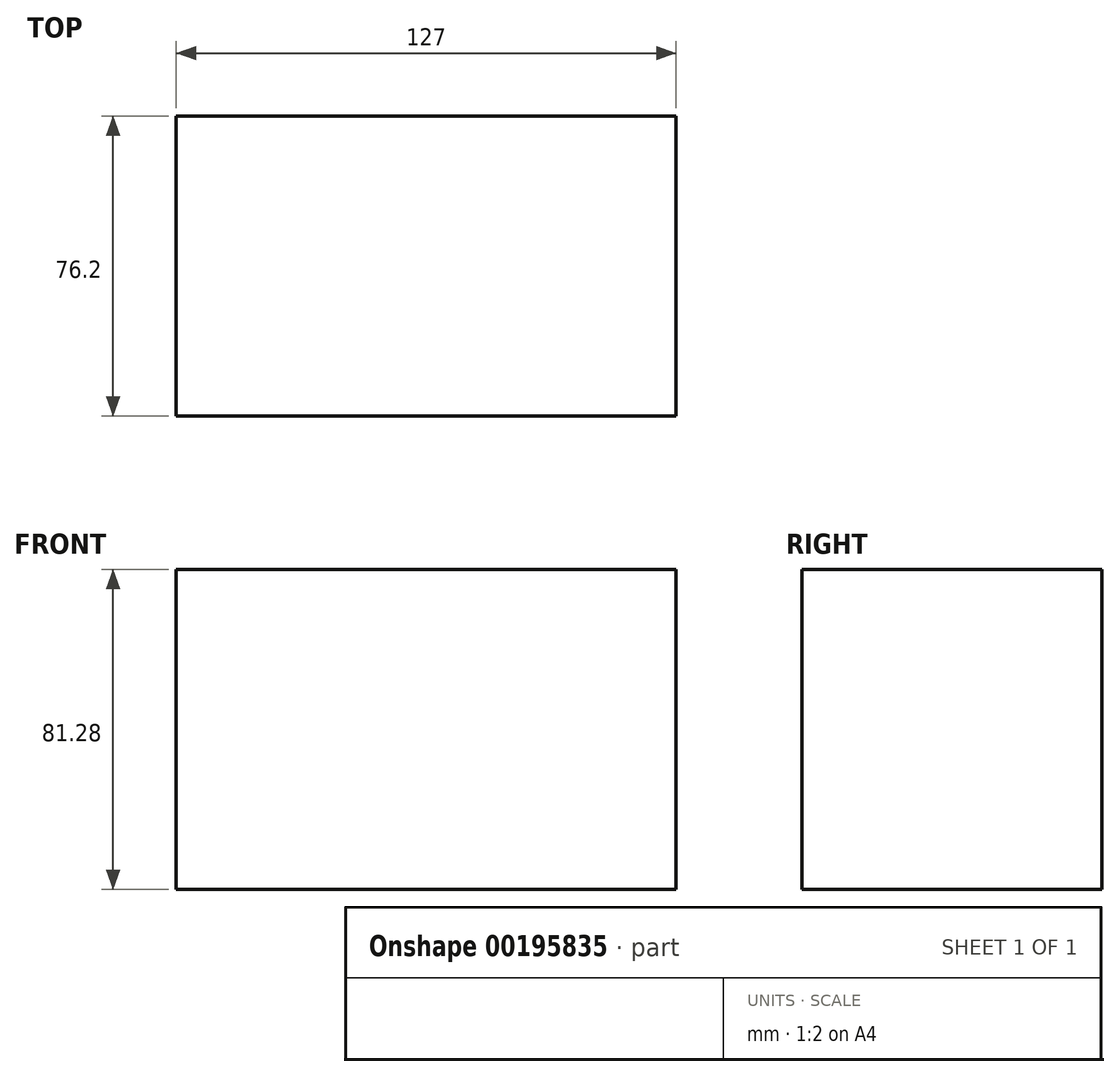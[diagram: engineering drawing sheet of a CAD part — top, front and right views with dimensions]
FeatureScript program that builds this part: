
annotation { "Feature Type Name" : "Feature", "Feature Type Description" : "" }
export const myFeature = defineFeature(function(context is Context, id is Id, definition is map)
    precondition{}
    {
        {
            var Q0;
            Q0=qCreatedBy(makeId("Top.planeOp"),FACE);
            var sketch = newSketch(context, id + "F0", { "sketchPlane" : qUnion([Q0])});
            skLineSegment(sketch, "E0.bottom", {"start": v(-63.5, 38.1) * mm, "end": v(63.5, 38.1) * mm});
            skLineSegment(sketch, "E0.top", {"start": v(-63.5, -38.1) * mm, "end": v(63.5, -38.1) * mm});
            skLineSegment(sketch, "E0.left", {"start": v(-63.5, 38.1) * mm, "end": v(-63.5, -38.1) * mm});
            skLineSegment(sketch, "E0.right", {"start": v(63.5, 38.1) * mm, "end": v(63.5, -38.1) * mm});
            skPoint(sketch, "E0.middle", {"position": v(0, 0) * mm});
            skSolve(sketch);
        }
        {
            var Q0;
            Q0=makeQuery(id+"F0.imprint","IMPRINT",FACE,{"disambiguationData":[TD([[makeQuery(id+"F0.imprint","IMPRINT",EDGE,{"derivedFrom":sQuery(id+"F0.wireOp",EDGE,"E0.bottom")}),-1.0]])]});
            extrude(context, id + "F1", {"entities" : qUnion([Q0]), "depth" : 81.28 * mm});
        }
    });
